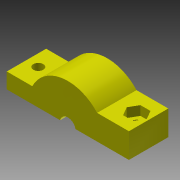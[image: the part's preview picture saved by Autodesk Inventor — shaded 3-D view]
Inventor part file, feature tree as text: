
AUTODESK INVENTOR PART (.ipt)
format: ipt  version: 2013 (Build 170138000, 138)  size: 133,632 bytes
history: native  units: in
note: dims shown in document units (in); Inventor stores cm internally (conversion verified against a paired STEP export)
features: extrude x4, sketch x4, projected_geometry x1
ambient origin geometry x8: Origin, YZ Plane, XZ Plane, XY Plane, X Axis, Y Axis, Z Axis, Center Point
bodies: Solid1 (feature_tree)
feature tree (9):
  extrude  "Extrusion1"  Depth=0.75in
  extrude  "Extrusion3"  Depth=0.1969in
  extrude  "Extrusion2"  Depth=0.5in TaperAngle=0.0deg
  extrude  "Extrusion5"  Depth=0.0625in TaperAngle=0.0deg
  sketch  "Sketch1"  dims[d0=0.2in d2=0.75in]
  sketch  "Sketch2"  dims[d3=0.0197in d4=0.1969in]
  sketch  "Sketch3"  dims[d5=0.625in d6=0.5in d7=0.0in]
  projected_geometry  "Projected Loop1"
  sketch  "Sketch6"  dims[d8=0.3125in d11=0.0625in d12=0.0in d13=0.126in d15=0.4688in d16=0.4688in d17=0.0625in d18=0.0in d30=0.2205in d31=0.1181in d32=0.0in]
